# Revit family: SLIM
name_source: partatom
category: Осветительные приборы
units: mm (PartAtom-declared; Revit-internal decimal feet)

## family parameters
Всегда вертикально = Нет
Источник света = Да
На основе рабочей плоскости = Да
Общий = Нет
При загрузке вырезать с полостями = Нет
Размер круглого соединителя = Использовать диаметр
Тип детали = Нормальный
Точка расчета площади = Да

## types (5) — shared parameters
ADSK_Единица измерения = шт.
ADSK_Завод-изготовитель = ЗАО «Центрстройсвет»
ADSK_Классификация нагрузок = Прочее
ADSK_Количество фаз = 1
ADSK_Количество фаз числовое = 1
ADSK_Коэффициент мощности = 0.92
ADSK_Масса = 1.5
ADSK_Напряжение = 230 В
ADSK_Номинальная мощность = 38 Вт
ADSK_Полная мощность = 41 В·А
ADSK_Ток = 0 А
URL = http://csvt.ru
l = 20 мм
Видимая форма излучения при визуализации = Да
Высота = 85 мм
Длина = 1262 мм
Изготовитель = ЗАО «Центрстройсвет»
Излучение по длине прямоугольника = 1222 мм
Излучение по ширине прямоугольника = 84 мм
Материал коробки = <По категории>
Материал светильника = RAL 9006
Материал стекла = RAL 9001
Отметка по умолчанию = 1219 мм
Светофильтр = 16777215
Смещение цветовой температуры при затухании лампы = <Нет>
Угол наклона = 90.00°
Ширина = 124 мм

## per-type parameters (varying)
| type | ADSK_Код изделия | ADSK_Наименование | ADSK_Обозначение | Файл фотометрической сетки |
| CSVT SLIM-38/опал (IP65, 5000К ) | ЦБ000008718 | Светодиодный пылевлагозащищенный светильник CSVT SLIM-38/опал (IP65, 5000К) | CSVT SLIM-38/опал (IP65, 5000К) | Светильник SLIM-38-opal.ies |
| CSVT SLIM-38/опал  (IP65, 5000К ) c БАП на 1 час. | ЦБ000008832 | Светодиодный пылевлагозащищенный светильник CSVT SLIM-38/опал  (IP65, 5000К ) c БАП на 1 час. | CSVT SLIM-38/опал  (IP65, 5000К ) | Светильник SLIM-38-opal.ies |
| CSVT Slim-38 (IP65, 5000К) | ЦБ000004227 | Светодиодный пылевлагозащищенный светильник CSVT Slim-38 (IP65, 5000К) | CSVT Slim-38 (IP65, 5000К) | Светильник SLIM-38-opal.ies |
| CSVT SLIM-38/MILKY  (IP65, 5000К ) | ЦБ000009202 | Светодиодный пылевлагозащищенный светильник CSVT SLIM-38/MILKY  (IP65, 5000К ) | CSVT SLIM-38/MILKY  (IP65, 5000К ) | CSVT Slim-38Milky.ies |
| CSVT SLIM-38/MILKY (IP65, 5000К ) c БАП на 1 час. | ЦБ000009203 | Светодиодный пылевлагозащищенный светильник CSVT SLIM-38/MILKY (IP65, 5000К ) c БАП на 1 час. | CSVT SLIM-38/MILKY  (IP65, 5000К ) | CSVT Slim-38Milky.ies |
